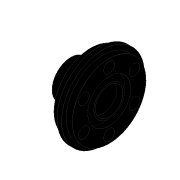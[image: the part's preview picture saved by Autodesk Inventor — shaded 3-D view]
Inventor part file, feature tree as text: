
AUTODESK INVENTOR PART (.ipt)
format: ipt  version: 2020 (Build 240168000, 168)  size: 403,968 bytes
history: native  units: in
note: dims shown in document units (in); Inventor stores cm internally (conversion verified against a paired STEP export)
features: extrude x8, sketch x8, projected_geometry x2, chamfer x1
ambient origin geometry x8: Origin, YZ Plane, XZ Plane, XY Plane, X Axis, Y Axis, Z Axis, Center Point
bodies: Solid1 (feature_tree)
feature tree (19):
  extrude  "Extrusion1"  Depth=0.3937in
  extrude  "Extrusion2"  Depth=0.1969in
  extrude  "Extrusion3"  Depth=0.7874in
  extrude  "Extrusion4"  Depth=0.0394in TaperAngle=0.0deg
  extrude  "Extrusion5"  Depth=0.1181in TaperAngle=0.0deg
  chamfer  "Chamfer1"  Distance=0.1181in
  extrude  "Extrusion6"  Depth=0.9843in
  extrude  "Extrusion7"  Depth=0.2756in
  extrude  "Extrusion8"  Depth=0.1969in TaperAngle=360.0deg
  sketch  "Sketch1"  dims[d0=1.8898in d1=0.3937in]
  sketch  "Sketch2"  dims[d2=0.1969in d3=0.2756in]
  projected_geometry  "Projected Loop1"
  sketch  "Sketch3"  dims[d4=2.3622in d6=360.0deg d8=0.7874in]
  projected_geometry  "Projected Loop2"
  sketch  "Sketch4"  dims[d9=0.0394in d10=0.1575in d11=0.0in]
  sketch  "Sketch5"  dims[d12=0.1181in d13=0.1181in d14=0.0in d15=0.1181in d16=0.0in]
  sketch  "Sketch6"  dims[d17=0.0787in d18=0.0in d19=0.9843in]
  sketch  "Sketch7"  dims[d20=0.2756in d21=0.0in d22=0.2756in d23=0.125in d24=0.0137in]
  sketch  "Sketch8"  dims[d25=0.0157in d26=2.3622in d28=360.0deg d30=0.2756in d31=0.0in d32=0.0394in d33=0.0in d35=0.0394in d36=0.0866in d37=0.0827in d38=0.0827in d39=0.0827in d40=5.9055in d42=360.0deg d44=0.1969in d45=0.0in]
